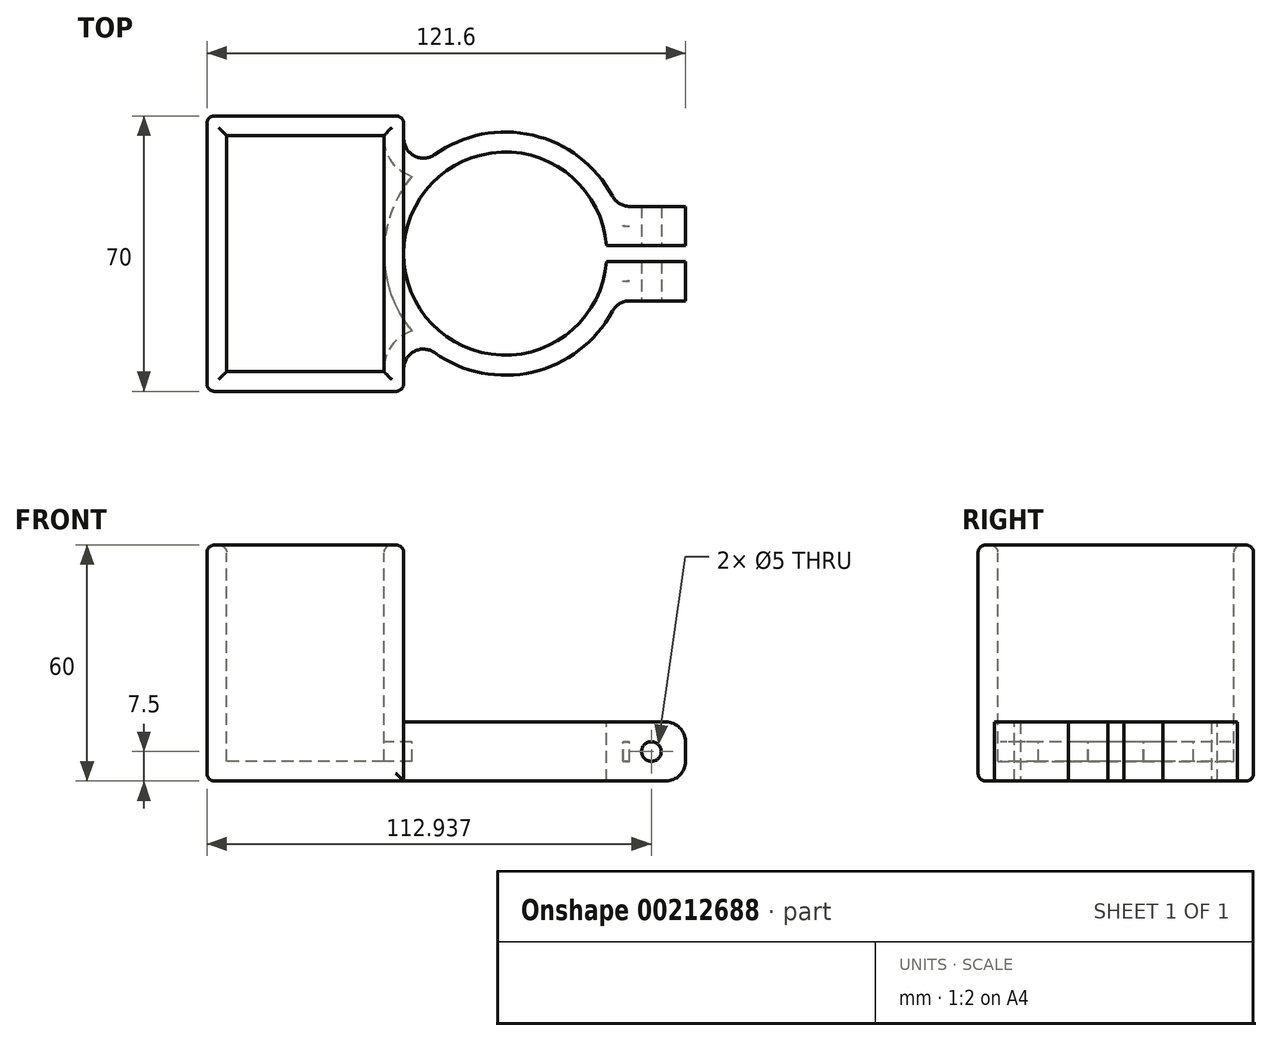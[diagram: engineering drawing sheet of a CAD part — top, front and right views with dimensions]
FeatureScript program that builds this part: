
annotation { "Feature Type Name" : "Feature", "Feature Type Description" : "" }
export const myFeature = defineFeature(function(context is Context, id is Id, definition is map)
    precondition{}
    {
        {
            assignVariable(context, id + "F0", {"name" : "strapHeight", "anyValue" : 15 * mm});
        }
        {
            assignVariable(context, id + "F1", {"name" : "tabThickness", "anyValue" : 12 * mm});
        }
        {
            var Q0;
            Q0=qCreatedBy(makeId("Top.planeOp"),FACE);
            var sketch = newSketch(context, id + "F2", { "sketchPlane" : qUnion([Q0])});
            skCircle(sketch, "E0", {"center": v(0, 0) * mm, "radius": 30.9 * mm});
            skSolve(sketch);
        }
        {
            var Q0;
            Q0 = qSketchRegion(id + "F2", true);
            extrude(context, id + "F3", {"entities" : qUnion([Q0]), "depth" : getVariable(context, 'strapHeight')});
        }
        {
            var Q0;
            Q0=makeQuery(id+"F3.opExtrude","CAP_FACE",FACE,{"disambiguationData":[OSD([sQuery(id+"F2.wireOp",EDGE,"E0")])],"isStart":false});
            var sketch = newSketch(context, id + "F4", { "sketchPlane" : qUnion([Q0])});
            skCircle(sketch, "E1", {"center": v(0, 0) * mm, "radius": 25.8 * mm});
            skSolve(sketch);
        }
        {
            var Q0;
            Q0 = qSketchRegion(id + "F4", true);
            extrude(context, id + "F5", {"entities" : qUnion([Q0]), "operationType" : NewBodyOperationType.REMOVE, "endBound" : BoundingType.THROUGH_ALL, "oppositeDirection" : true, "depth" : 25 * mm});
        }
        {
            var Q0;
            Q0=qCreatedBy(makeId("Front.planeOp"),FACE);
            var sketch = newSketch(context, id + "F6", { "sketchPlane" : qUnion([Q0])});
            skLineSegment(sketch, "E2.0", {"start": v(-25.8, 15) * mm, "end": v(25.8, 15) * mm, "construction": true});
            skLineSegment(sketch, "E3.bottom", {"start": v(25.8, 15) * mm, "end": v(45.8, 15) * mm});
            skLineSegment(sketch, "E3.top", {"start": v(25.8, 0) * mm, "end": v(45.8, 0) * mm});
            skLineSegment(sketch, "E3.left", {"start": v(25.8, 15) * mm, "end": v(25.8, 0) * mm});
            skLineSegment(sketch, "E3.right", {"start": v(45.8, 15) * mm, "end": v(45.8, 0) * mm});
            skSolve(sketch);
        }
        {
            var Q0;
            Q0 = qSketchRegion(id + "F6", true);
            extrude(context, id + "F7", {"entities" : qUnion([Q0]), "operationType" : NewBodyOperationType.ADD, "depth" : getVariable(context, 'tabThickness'), "hasSecondDirection" : true, "secondDirectionOppositeDirection" : true, "secondDirectionDepth" : getVariable(context, 'tabThickness')});
        }
        {
            var Q0;
            Q0=makeQuery(id+"F7.opExtrude","CAP_FACE",FACE,{"disambiguationData":[OSD([sQuery(id+"F6.wireOp",EDGE,"E3.bottom"),sQuery(id+"F6.wireOp",EDGE,"E3.top"),sQuery(id+"F6.wireOp",EDGE,"E3.left"),sQuery(id+"F6.wireOp",EDGE,"E3.right")])],"isStart":false});
            var sketch = newSketch(context, id + "F8", { "sketchPlane" : qUnion([Q0])});
            skLineSegment(sketch, "E4", {"start": v(45.8, 7.5) * mm, "end": v(28.47, 7.5) * mm, "construction": true});
            skLineSegment(sketch, "E5", {"start": v(37.14, 15) * mm, "end": v(37.14, 0) * mm, "construction": true});
            skCircle(sketch, "E6", {"center": v(37.14, 7.5) * mm, "radius": 2.5 * mm});
            skSolve(sketch);
        }
        {
            var Q0;
            Q0 = qSketchRegion(id + "F8", true);
            extrude(context, id + "F9", {"entities" : qUnion([Q0]), "operationType" : NewBodyOperationType.REMOVE, "endBound" : BoundingType.THROUGH_ALL, "oppositeDirection" : true, "depth" : 25 * mm});
        }
        {
            var Q0;
            Q0=qCreatedBy(makeId("Front.planeOp"),FACE);
            var sketch = newSketch(context, id + "F10", { "sketchPlane" : qUnion([Q0])});
            skCircle(sketch, "E7", {"center": v(36.91, 7.6) * mm, "radius": 15.66 * mm});
            skSolve(sketch);
        }
        {
            var Q0;
            Q0 = qSketchRegion(id + "F10", true);
            extrude(context, id + "F11", {"entities" : qUnion([Q0]), "operationType" : NewBodyOperationType.REMOVE, "oppositeDirection" : true, "depth" : 2 * mm, "hasSecondDirection" : true, "secondDirectionOppositeDirection" : false, "secondDirectionDepth" : 2 * mm});
        }
        {
            var Q0;
            Q0=qCreatedBy(makeId("Front.planeOp"),FACE);
            var sketch = newSketch(context, id + "F12", { "sketchPlane" : qUnion([Q0])});
            skLineSegment(sketch, "E8.0", {"start": v(25.72, 0) * mm, "end": v(-25.8, 0) * mm, "construction": true});
            skLineSegment(sketch, "E9.bottom", {"start": v(-25.8, 0) * mm, "end": v(-75.8, 0) * mm});
            skLineSegment(sketch, "E9.top", {"start": v(-25.8, 60) * mm, "end": v(-75.8, 60) * mm});
            skLineSegment(sketch, "E9.left", {"start": v(-25.8, 0) * mm, "end": v(-25.8, 60) * mm});
            skLineSegment(sketch, "E9.right", {"start": v(-75.8, 0) * mm, "end": v(-75.8, 60) * mm});
            skSolve(sketch);
        }
        {
            var Q0;
            Q0 = qSketchRegion(id + "F12", true);
            extrude(context, id + "F13", {"entities" : qUnion([Q0]), "operationType" : NewBodyOperationType.ADD, "depth" : 35 * mm, "hasSecondDirection" : true, "secondDirectionOppositeDirection" : true, "secondDirectionDepth" : 35 * mm});
        }
        {
            var Q0;
            {var subQ0=sQuery(id+"F6.wireOp",EDGE,"E3.right");var subQ1=sQuery(id+"F6.wireOp",EDGE,"E3.bottom");Q0=makeQuery(id+"F11.boolean.opBoolean","SPLIT",EDGE,{"disambiguationData":[TD([makeQuery(id+"F11.opExtrude","CAP_FACE",FACE,{"disambiguationData":[OSD([sQuery(id+"F10.wireOp",EDGE,"E7")])],"isStart":true})])],"derivedFrom":makeQuery(id+"F7.opExtrude","SWEPT_EDGE",EDGE,{"disambiguationData":[OSD([subQ1,subQ0])]})});}
            var Q1;
            {var subQ0=sQuery(id+"F6.wireOp",EDGE,"E3.right");var subQ1=sQuery(id+"F6.wireOp",EDGE,"E3.bottom");Q1=makeQuery(id+"F11.boolean.opBoolean","SPLIT",EDGE,{"disambiguationData":[TD([makeQuery(id+"F11.opExtrude","CAP_FACE",FACE,{"disambiguationData":[OSD([sQuery(id+"F10.wireOp",EDGE,"E7")])],"isStart":false})])],"derivedFrom":makeQuery(id+"F7.opExtrude","SWEPT_EDGE",EDGE,{"disambiguationData":[OSD([subQ1,subQ0])]})});}
            var Q2;
            {var subQ0=sQuery(id+"F6.wireOp",EDGE,"E3.top");var subQ1=sQuery(id+"F6.wireOp",EDGE,"E3.right");Q2=makeQuery(id+"F11.boolean.opBoolean","SPLIT",EDGE,{"disambiguationData":[TD([makeQuery(id+"F11.opExtrude","CAP_FACE",FACE,{"disambiguationData":[OSD([sQuery(id+"F10.wireOp",EDGE,"E7")])],"isStart":false})])],"derivedFrom":makeQuery(id+"F7.opExtrude","SWEPT_EDGE",EDGE,{"disambiguationData":[OSD([subQ0,subQ1])]})});}
            var Q3;
            {var subQ0=sQuery(id+"F6.wireOp",EDGE,"E3.right");var subQ1=sQuery(id+"F6.wireOp",EDGE,"E3.top");Q3=makeQuery(id+"F11.boolean.opBoolean","SPLIT",EDGE,{"disambiguationData":[TD([makeQuery(id+"F11.opExtrude","CAP_FACE",FACE,{"disambiguationData":[OSD([sQuery(id+"F10.wireOp",EDGE,"E7")])],"isStart":true})])],"derivedFrom":makeQuery(id+"F7.opExtrude","SWEPT_EDGE",EDGE,{"disambiguationData":[OSD([subQ1,subQ0])]})});}
            var Q4;
            Q4=makeQuery(id+"F7.boolean.opBoolean","INTERSECT",EDGE,{"derivedFrom":[makeQuery(id+"F3.opExtrude","SWEPT_FACE",FACE,{"disambiguationData":[OSD([sQuery(id+"F2.wireOp",EDGE,"E0")])]}),makeQuery(id+"F7.opExtrude","CAP_FACE",FACE,{"disambiguationData":[OSD([sQuery(id+"F6.wireOp",EDGE,"E3.bottom"),sQuery(id+"F6.wireOp",EDGE,"E3.top"),sQuery(id+"F6.wireOp",EDGE,"E3.left"),sQuery(id+"F6.wireOp",EDGE,"E3.right")])],"isStart":false})]});
            var Q5;
            Q5=makeQuery(id+"F7.boolean.opBoolean","INTERSECT",EDGE,{"derivedFrom":[makeQuery(id+"F3.opExtrude","SWEPT_FACE",FACE,{"disambiguationData":[OSD([sQuery(id+"F2.wireOp",EDGE,"E0")])]}),makeQuery(id+"F7.opExtrude","CAP_FACE",FACE,{"disambiguationData":[OSD([sQuery(id+"F6.wireOp",EDGE,"E3.bottom"),sQuery(id+"F6.wireOp",EDGE,"E3.top"),sQuery(id+"F6.wireOp",EDGE,"E3.left"),sQuery(id+"F6.wireOp",EDGE,"E3.right")])],"isStart":true})]});
            var Q6;
            Q6=makeQuery(id+"F13.boolean.opBoolean","INTERSECT",EDGE,{"disambiguationData":[OD(1.0)],"derivedFrom":[makeQuery(id+"F3.opExtrude","SWEPT_FACE",FACE,{"disambiguationData":[OSD([sQuery(id+"F2.wireOp",EDGE,"E0")])]}),makeQuery(id+"F13.opExtrude","SWEPT_FACE",FACE,{"disambiguationData":[OSD([sQuery(id+"F12.wireOp",EDGE,"E9.left")])]})]});
            var Q7;
            Q7=makeQuery(id+"F13.boolean.opBoolean","INTERSECT",EDGE,{"disambiguationData":[OD(0.0)],"derivedFrom":[makeQuery(id+"F3.opExtrude","SWEPT_FACE",FACE,{"disambiguationData":[OSD([sQuery(id+"F2.wireOp",EDGE,"E0")])]}),makeQuery(id+"F13.opExtrude","SWEPT_FACE",FACE,{"disambiguationData":[OSD([sQuery(id+"F12.wireOp",EDGE,"E9.left")])]})]});
            fillet(context, id + "F14", {"entities" : qUnion([Q0, Q1, Q2, Q3, Q4, Q5, Q6, Q7]), "radius" : 5 * mm, "tangentPropagation" : true, "allowEdgeOverflow" : false});
        }
        {
            var Q0;
            Q0=makeQuery(id+"F13.opExtrude","SWEPT_FACE",FACE,{"disambiguationData":[OSD([sQuery(id+"F12.wireOp",EDGE,"E9.top")])]});
            shell(context, id + "F15", {"entities" : qUnion([Q0]), "thickness" : 5 * mm});
        }
        {
            var Q0;
            Q0=makeQuery(id+"F13.opExtrude","SWEPT_FACE",FACE,{"disambiguationData":[OSD([sQuery(id+"F12.wireOp",EDGE,"E9.top")])]});
            var Q1;
            Q1=makeQuery(id+"F13.opExtrude","CAP_FACE",FACE,{"disambiguationData":[OSD([sQuery(id+"F12.wireOp",EDGE,"E9.bottom"),sQuery(id+"F12.wireOp",EDGE,"E9.top"),sQuery(id+"F12.wireOp",EDGE,"E9.left"),sQuery(id+"F12.wireOp",EDGE,"E9.right")])],"isStart":false});
            var Q2;
            Q2=makeQuery(id+"F13.opExtrude","SWEPT_FACE",FACE,{"disambiguationData":[OSD([sQuery(id+"F12.wireOp",EDGE,"E9.right")])]});
            var Q3;
            Q3=makeQuery(id+"F13.opExtrude","CAP_FACE",FACE,{"disambiguationData":[OSD([sQuery(id+"F12.wireOp",EDGE,"E9.bottom"),sQuery(id+"F12.wireOp",EDGE,"E9.top"),sQuery(id+"F12.wireOp",EDGE,"E9.left"),sQuery(id+"F12.wireOp",EDGE,"E9.right")])],"isStart":true});
            fillet(context, id + "F16", {"entities" : qUnion([Q0, Q1, Q2, Q3]), "radius" : 2 * mm, "tangentPropagation" : true, "allowEdgeOverflow" : false});
        }
    });
